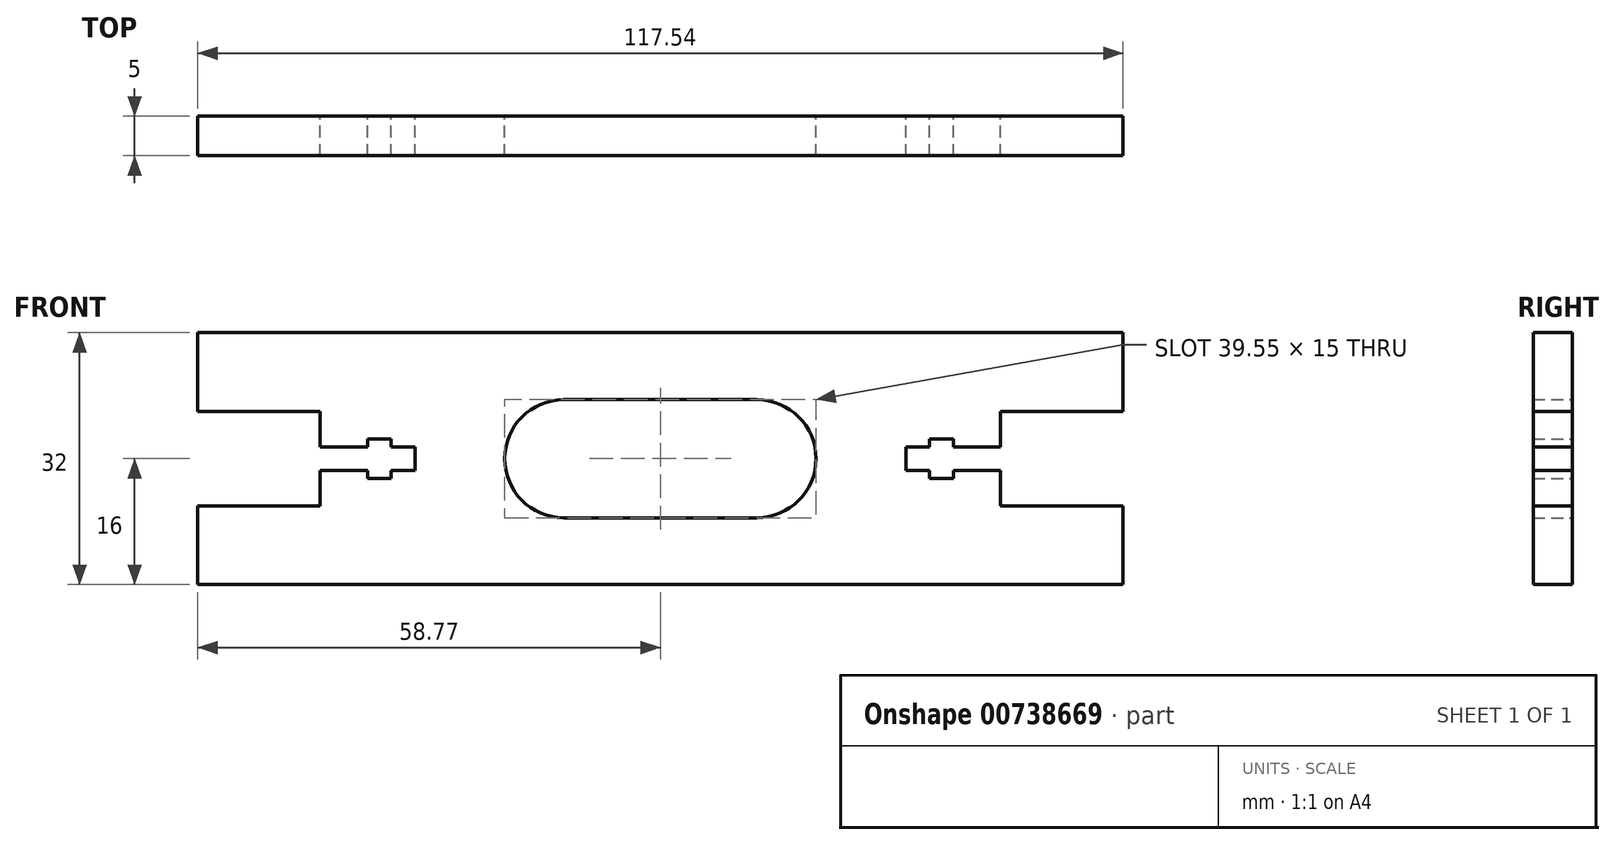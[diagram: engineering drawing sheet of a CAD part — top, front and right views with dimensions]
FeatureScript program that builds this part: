
annotation { "Feature Type Name" : "Feature", "Feature Type Description" : "" }
export const myFeature = defineFeature(function(context is Context, id is Id, definition is map)
    precondition{}
    {
        {
            var Q0;
            Q0=qCreatedBy(makeId("Front.planeOp"),FACE);
            var sketch = newSketch(context, id + "F0", { "sketchPlane" : qUnion([Q0])});
            skLineSegment(sketch, "E0", {"start": v(0, -16) * mm, "end": v(58.77, -16) * mm});
            skLineSegment(sketch, "E1", {"start": v(58.77, -16) * mm, "end": v(58.77, -6) * mm});
            skLineSegment(sketch, "E2", {"start": v(58.77, -6) * mm, "end": v(43.21, -6) * mm});
            skLineSegment(sketch, "E3", {"start": v(43.21, -6) * mm, "end": v(43.21, -1.5) * mm});
            skLineSegment(sketch, "E4", {"start": v(0, -16) * mm, "end": v(0, 0) * mm, "construction": true});
            skLineSegment(sketch, "E5", {"start": v(0, 0) * mm, "end": v(43.21, 0) * mm, "construction": true});
            skLineSegment(sketch, "E6.MirrorCS", {"start": v(43.21, 6) * mm, "end": v(43.21, 1.5) * mm});
            skLineSegment(sketch, "E7.MirrorCS", {"start": v(58.77, 6) * mm, "end": v(43.21, 6) * mm});
            skLineSegment(sketch, "E8.MirrorCS", {"start": v(58.77, 16) * mm, "end": v(58.77, 6) * mm});
            skLineSegment(sketch, "E9.MirrorCS", {"start": v(0, 16) * mm, "end": v(58.77, 16) * mm});
            skLineSegment(sketch, "E10.MirrorCS", {"start": v(0, 16) * mm, "end": v(0, 0) * mm, "construction": true});
            skLineSegment(sketch, "E11", {"start": v(43.21, 1.5) * mm, "end": v(37.21, 1.5) * mm});
            skLineSegment(sketch, "E12", {"start": v(37.21, 1.5) * mm, "end": v(37.21, 2.5) * mm});
            skLineSegment(sketch, "E13", {"start": v(37.21, 2.5) * mm, "end": v(34.21, 2.5) * mm});
            skLineSegment(sketch, "E14", {"start": v(34.21, 2.5) * mm, "end": v(34.21, 1.5) * mm});
            skLineSegment(sketch, "E15", {"start": v(34.21, 1.5) * mm, "end": v(31.17, 1.5) * mm});
            skLineSegment(sketch, "E16", {"start": v(31.17, 1.5) * mm, "end": v(31.17, 0) * mm});
            skLineSegment(sketch, "E17.MirrorCS", {"start": v(62.34, 0) * mm, "end": v(19.12, 0) * mm, "construction": true});
            skLineSegment(sketch, "E18.MirrorCS", {"start": v(34.21, -2.5) * mm, "end": v(34.21, -1.5) * mm});
            skLineSegment(sketch, "E19.MirrorCS", {"start": v(37.21, -1.5) * mm, "end": v(37.21, -2.5) * mm});
            skLineSegment(sketch, "E20.MirrorCS", {"start": v(34.21, -1.5) * mm, "end": v(31.17, -1.5) * mm});
            skLineSegment(sketch, "E21.MirrorCS", {"start": v(31.17, -1.5) * mm, "end": v(31.17, 0) * mm});
            skLineSegment(sketch, "E22.MirrorCS", {"start": v(37.21, -2.5) * mm, "end": v(34.21, -2.5) * mm});
            skLineSegment(sketch, "E23.MirrorCS", {"start": v(43.21, -1.5) * mm, "end": v(37.21, -1.5) * mm});
            skPoint(sketch, "E24.orphan", {"position": v(43.21, 0) * mm});
            skArc(sketch, "E25", {"start": v(12.27, -7.5) * mm, "mid": v(19.77, 0) * mm, "end": v(12.27, 7.5) * mm});
            skLineSegment(sketch, "E26", {"start": v(12.27, 7.5) * mm, "end": v(0, 7.5) * mm});
            skLineSegment(sketch, "E27", {"start": v(12.27, -7.5) * mm, "end": v(0, -7.5) * mm});
            skLineSegment(sketch, "E28.MirrorCS", {"start": v(-31.17, 1.5) * mm, "end": v(-31.17, 0) * mm});
            skLineSegment(sketch, "E29.MirrorCS", {"start": v(-34.21, -2.5) * mm, "end": v(-34.21, -1.5) * mm});
            skLineSegment(sketch, "E30.MirrorCS", {"start": v(-37.21, 2.5) * mm, "end": v(-34.21, 2.5) * mm});
            skLineSegment(sketch, "E31.MirrorCS", {"start": v(-34.21, 2.5) * mm, "end": v(-34.21, 1.5) * mm});
            skLineSegment(sketch, "E32.MirrorCS", {"start": v(-37.21, -1.5) * mm, "end": v(-37.21, -2.5) * mm});
            skLineSegment(sketch, "E33.MirrorCS", {"start": v(-31.17, -1.5) * mm, "end": v(-31.17, 0) * mm});
            skLineSegment(sketch, "E34.MirrorCS", {"start": v(-37.21, 1.5) * mm, "end": v(-37.21, 2.5) * mm});
            skLineSegment(sketch, "E35.MirrorCS", {"start": v(-37.21, -2.5) * mm, "end": v(-34.21, -2.5) * mm});
            skLineSegment(sketch, "E36.MirrorCS", {"start": v(-34.21, 1.5) * mm, "end": v(-31.17, 1.5) * mm});
            skLineSegment(sketch, "E37.MirrorCS", {"start": v(-43.21, 1.5) * mm, "end": v(-37.21, 1.5) * mm});
            skLineSegment(sketch, "E38.MirrorCS", {"start": v(-34.21, -1.5) * mm, "end": v(-31.17, -1.5) * mm});
            skLineSegment(sketch, "E39.MirrorCS", {"start": v(-62.34, 0) * mm, "end": v(-19.12, 0) * mm, "construction": true});
            skLineSegment(sketch, "E40.MirrorCS", {"start": v(-58.77, 6) * mm, "end": v(-43.21, 6) * mm});
            skLineSegment(sketch, "E41.MirrorCS", {"start": v(-43.21, 6) * mm, "end": v(-43.21, 1.5) * mm});
            skArc(sketch, "E42.MirrorCS", {"start": v(-12.27, -7.5) * mm, "mid": v(-19.77, 0) * mm, "end": v(-12.27, 7.5) * mm});
            skLineSegment(sketch, "E43.MirrorCS", {"start": v(-58.77, 16) * mm, "end": v(-58.77, 6) * mm});
            skPoint(sketch, "E44.MirrorP", {"position": v(-43.21, 0) * mm});
            skLineSegment(sketch, "E45.MirrorCS", {"start": v(0, 16) * mm, "end": v(-58.77, 16) * mm});
            skLineSegment(sketch, "E46.MirrorCS", {"start": v(0, 0) * mm, "end": v(-43.21, 0) * mm, "construction": true});
            skLineSegment(sketch, "E47.MirrorCS", {"start": v(-12.27, -7.5) * mm, "end": v(0, -7.5) * mm});
            skLineSegment(sketch, "E48.MirrorCS", {"start": v(-43.21, -1.5) * mm, "end": v(-37.21, -1.5) * mm});
            skLineSegment(sketch, "E49.MirrorCS", {"start": v(-12.27, 7.5) * mm, "end": v(0, 7.5) * mm});
            skLineSegment(sketch, "E50.MirrorCS", {"start": v(-43.21, -6) * mm, "end": v(-43.21, -1.5) * mm});
            skLineSegment(sketch, "E51.MirrorCS", {"start": v(0, -16) * mm, "end": v(-58.77, -16) * mm});
            skLineSegment(sketch, "E52.MirrorCS", {"start": v(-58.77, -6) * mm, "end": v(-43.21, -6) * mm});
            skLineSegment(sketch, "E53.MirrorCS", {"start": v(-58.77, -16) * mm, "end": v(-58.77, -6) * mm});
            skSolve(sketch);
        }
        {
            var Q0;
            Q0 = qSketchRegion(id + "F0", true);
            extrude(context, id + "F1", {"entities" : qUnion([Q0]), "depth" : 5 * mm, "offsetDistance" : 25 * mm});
        }
    });
